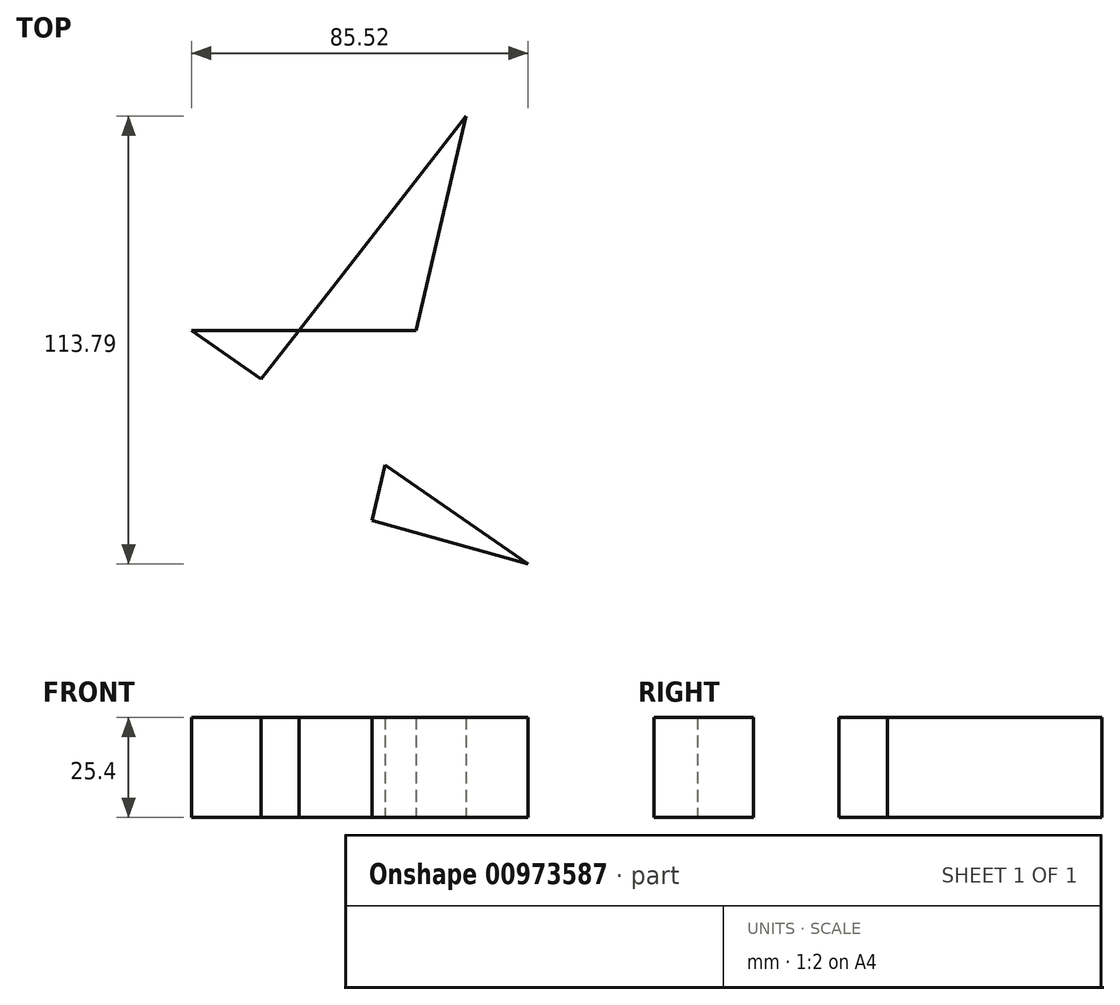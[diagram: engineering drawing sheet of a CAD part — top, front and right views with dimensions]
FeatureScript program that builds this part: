
annotation { "Feature Type Name" : "Feature", "Feature Type Description" : "" }
export const myFeature = defineFeature(function(context is Context, id is Id, definition is map)
    precondition{}
    {
        {
            var Q0;
            Q0=qCreatedBy(makeId("Top.planeOp"),FACE);
            var sketch = newSketch(context, id + "F0", { "sketchPlane" : qUnion([Q0])});
            skLineSegment(sketch, "E0", {"start": v(45.02, 15.49) * mm, "end": v(-39.4, 15.49) * mm});
            skLineSegment(sketch, "E1", {"start": v(-39.4, 15.49) * mm, "end": v(46.12, -43.77) * mm});
            skLineSegment(sketch, "E2", {"start": v(46.12, -43.77) * mm, "end": v(-39.76, -19.96) * mm});
            skLineSegment(sketch, "E3", {"start": v(-39.76, -19.96) * mm, "end": v(30.4, 70.02) * mm});
            skLineSegment(sketch, "E4", {"start": v(30.4, 70.02) * mm, "end": v(5.92, -34.96) * mm});
            skSolve(sketch);
        }
        {
            var Q0;
            {var subQ0=sQuery(id+"F0.wireOp",EDGE,"E2");var subQ1=sQuery(id+"F0.wireOp",EDGE,"E1");var subQ2=makeQuery(id+"F0.imprint","INTERSECT",VERTEX,{"derivedFrom":[subQ1,subQ0]});Q0=makeQuery(id+"F0.imprint","IMPRINT",FACE,{"disambiguationData":[TD([[makeQuery(id+"F0.imprint","IMPRINT",EDGE,{"disambiguationData":[TD([[subQ2,1.0]])],"derivedFrom":subQ1}),-1.0]])]});}
            var Q1;
            {var subQ0=sQuery(id+"F0.wireOp",EDGE,"E1");var subQ1=sQuery(id+"F0.wireOp",EDGE,"E0");var subQ2=makeQuery(id+"F0.imprint","INTERSECT",VERTEX,{"derivedFrom":[subQ1,subQ0]});Q1=makeQuery(id+"F0.imprint","IMPRINT",FACE,{"disambiguationData":[TD([[makeQuery(id+"F0.imprint","IMPRINT",EDGE,{"disambiguationData":[TD([[subQ2,1.0]])],"derivedFrom":subQ1}),1.0]])]});}
            var Q2;
            {var subQ0=sQuery(id+"F0.wireOp",EDGE,"E4");var subQ1=sQuery(id+"F0.wireOp",EDGE,"E0");var subQ2=makeQuery(id+"F0.imprint","INTERSECT",VERTEX,{"derivedFrom":[subQ1,subQ0]});Q2=makeQuery(id+"F0.imprint","IMPRINT",FACE,{"disambiguationData":[TD([[makeQuery(id+"F0.imprint","IMPRINT",EDGE,{"disambiguationData":[TD([[subQ2,-1.0]])],"derivedFrom":subQ1}),-1.0]])]});}
            extrude(context, id + "F1", {"entities" : qUnion([Q0, Q1, Q2]), "depth" : 25.4 * mm, "offsetDistance" : 25.4 * mm});
        }
    });
